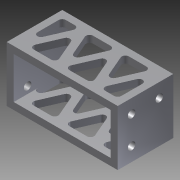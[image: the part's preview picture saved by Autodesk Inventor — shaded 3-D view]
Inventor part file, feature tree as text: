
AUTODESK INVENTOR PART (.ipt)
format: ipt  version: 2012 (Build 160160000, 160)  size: 238,080 bytes
history: native  units: in
note: dims shown in document units (in); Inventor stores cm internally (conversion verified against a paired STEP export)
features: extrude x3, sketch x3, fillet x2
ambient origin geometry x8: Origin, YZ Plane, XZ Plane, XY Plane, X Axis, Y Axis, Z Axis, Center Point
bodies: Solid1 (feature_tree)
feature tree (8):
  extrude  "Extrusion1"  Depth=1.0in
  extrude  "Extrusion2"  Depth=0.125in
  fillet  "Fillet1"  Radius=0.125in
  fillet  "Fillet2"  Radius=0.125in
  extrude  "Extrusion3"  Depth=0.125in
  sketch  "Sketch1"  dims[d0=2.0in d1=1.0in]
  sketch  "Sketch2"  dims[d2=0.125in d3=0.125in d4=0.125in d5=0.125in]
  sketch  "Sketch3"  dims[d6=1.0in d7=0.0in d9=0.0625in d10=0.125in d11=0.0625in d12=0.125in d13=0.0625in d14=0.125in d15=0.0625in d16=0.125in d17=0.0625in d18=0.125in d19=0.16in d20=0.32in d21=0.32in d22=0.32in d23=0.32in d24=0.125in d26=0.125in d27=0.125in d28=3.0in d29=0.0in d30=0.0625in d31=0.0625in d32=0.125in d33=0.136in d34=0.25in d35=0.25in d36=0.25in d37=0.25in d38=1.0in d39=0.0in]
